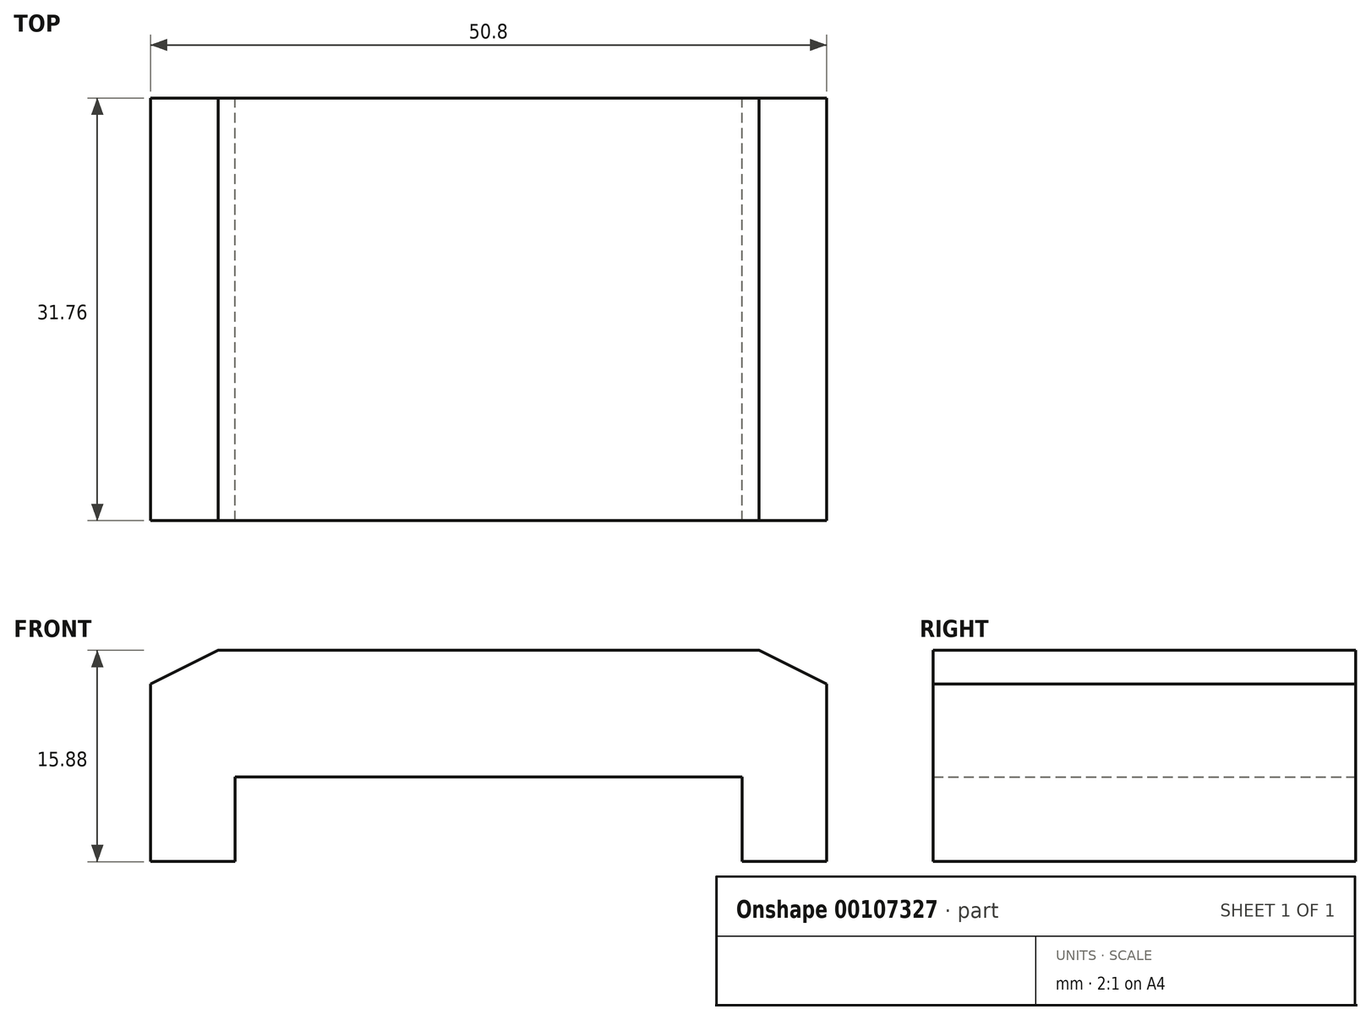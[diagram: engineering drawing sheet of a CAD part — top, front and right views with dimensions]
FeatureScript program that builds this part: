
annotation { "Feature Type Name" : "Feature", "Feature Type Description" : "" }
export const myFeature = defineFeature(function(context is Context, id is Id, definition is map)
    precondition{}
    {
        {
            var Q0;
            Q0=qCreatedBy(makeId("Top.planeOp"),FACE);
            var sketch = newSketch(context, id + "F0", { "sketchPlane" : qUnion([Q0])});
            skLineSegment(sketch, "E0.bottom", {"start": v(25.4, 15.88) * mm, "end": v(-25.4, 15.88) * mm});
            skLineSegment(sketch, "E0.top", {"start": v(25.4, -15.88) * mm, "end": v(-25.4, -15.88) * mm});
            skLineSegment(sketch, "E0.left", {"start": v(25.4, 15.88) * mm, "end": v(25.4, -15.88) * mm});
            skLineSegment(sketch, "E0.right", {"start": v(-25.4, 15.88) * mm, "end": v(-25.4, -15.88) * mm});
            skPoint(sketch, "E0.middle", {"position": v(0, 0) * mm});
            skSolve(sketch);
        }
        {
            var Q0;
            Q0=makeQuery(id+"F0.imprint","IMPRINT",FACE,{"disambiguationData":[TD([[makeQuery(id+"F0.imprint","IMPRINT",EDGE,{"derivedFrom":sQuery(id+"F0.wireOp",EDGE,"E0.bottom")}),1.0]])]});
            extrude(context, id + "F1", {"entities" : qUnion([Q0]), "oppositeDirection" : true, "depth" : 15.88 * mm});
        }
        {
            var Q0;
            Q0=makeQuery(id+"F1.opExtrude","CAP_FACE",FACE,{"disambiguationData":[OSD([sQuery(id+"F0.wireOp",EDGE,"E0.bottom"),sQuery(id+"F0.wireOp",EDGE,"E0.top"),sQuery(id+"F0.wireOp",EDGE,"E0.left"),sQuery(id+"F0.wireOp",EDGE,"E0.right")])],"isStart":false});
            var sketch = newSketch(context, id + "F2", { "sketchPlane" : qUnion([Q0])});
            skLineSegment(sketch, "E1.bottom", {"start": v(19.05, 15.88) * mm, "end": v(-19.05, 15.88) * mm});
            skLineSegment(sketch, "E1.top", {"start": v(19.05, -15.88) * mm, "end": v(-19.05, -15.88) * mm});
            skLineSegment(sketch, "E1.left", {"start": v(19.05, 15.88) * mm, "end": v(19.05, -15.88) * mm});
            skLineSegment(sketch, "E1.right", {"start": v(-19.05, 15.88) * mm, "end": v(-19.05, -15.88) * mm});
            skPoint(sketch, "E1.middle", {"position": v(0, 0) * mm});
            skSolve(sketch);
        }
        {
            var Q0;
            Q0=makeQuery(id+"F2.imprint","IMPRINT",FACE,{"disambiguationData":[TD([[makeQuery(id+"F2.imprint","IMPRINT",EDGE,{"derivedFrom":sQuery(id+"F2.wireOp",EDGE,"E1.bottom")}),1.0]])]});
            extrude(context, id + "F3", {"entities" : qUnion([Q0]), "operationType" : NewBodyOperationType.REMOVE, "oppositeDirection" : true, "depth" : 6.35 * mm});
        }
        {
            var Q0;
            Q0=makeQuery(id+"F1.opExtrude","CAP_EDGE",EDGE,{"disambiguationData":[OSD([sQuery(id+"F0.wireOp",EDGE,"E0.right")])],"isStart":true});
            var Q1;
            Q1=makeQuery(id+"F1.opExtrude","CAP_EDGE",EDGE,{"disambiguationData":[OSD([sQuery(id+"F0.wireOp",EDGE,"E0.left")])],"isStart":true});
            chamfer(context, id + "F4", {"entities" : qUnion([Q0, Q1]), "chamferType" : ChamferType.TWO_OFFSETS, "width1" : 2.54 * mm, "oppositeDirection" : true, "width2" : 5.08 * mm, "tangentPropagation" : true});
        }
    });
